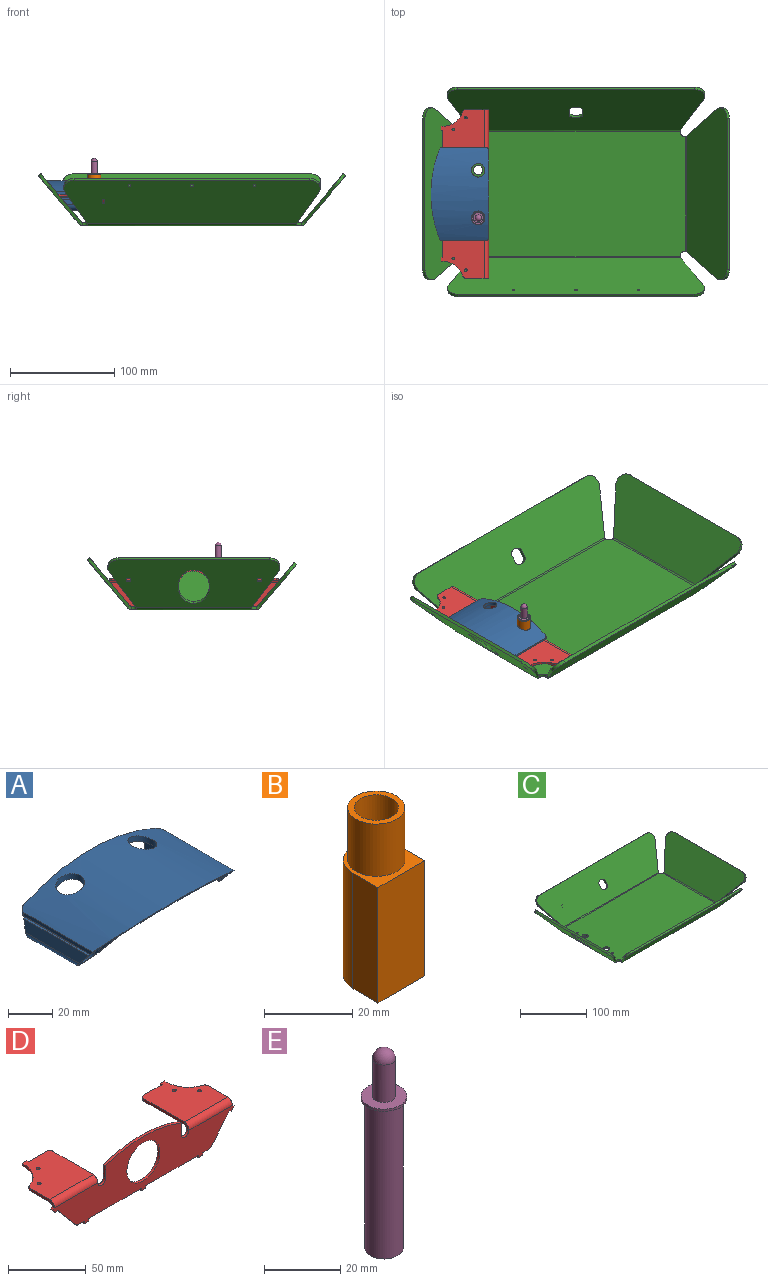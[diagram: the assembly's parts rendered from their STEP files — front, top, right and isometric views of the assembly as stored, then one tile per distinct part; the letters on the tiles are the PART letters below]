
ASSEMBLY  parts=5 mates=4
PART A: 54 faces, bbox 90.1x55.7x28.5 mm
  f0: plane 12.62x12mm, normal (-1,0,0), area 123.6mm2, adj f11,f12,f14,f30,f36,f42,f46,f48
  f1: plane 10x3.5mm, normal (0,0,-1), area 35mm2, adj f8,f13,f46,f47
  f2: plane 40.48x4mm, normal (1,0,0), area 99.5mm2, adj f3,f13,f31,f44,f46,f47
  f3: plane 90.07x28.52mm, normal (0,-0.77,-0.64), area 495.1mm2, adj f2,f15,f16,f17,f18,f19,f20,f21
  f4: cylinder r=1.5mm len=12mm, axis (0,1,0), area 56.5mm2, adj f5,f10,f42,f46
  f5: plane 12x2.1mm, normal (1,0,0), area 25.2mm2, adj f4,f6,f42,f46
  f6: cylinder r=1.5mm len=12mm, axis (0,1,0), area 22.2mm2, adj f5,f7,f42,f46
  f7: plane 12x4.99mm, normal (1,0,0), area 55.6mm2, adj f6,f11,f12,f42,f46,f48
  f8: plane 12x4.99mm, normal (-1,0,0), area 55.6mm2, adj f1,f9,f13,f41,f42,f46
  f9: cylinder r=1.5mm len=12mm, axis (0,1,0), area 22.2mm2, adj f8,f10,f42,f46
  f10: plane 12x2.1mm, normal (-1,0,0), area 25.2mm2, adj f4,f9,f42,f46
  f11: plane 5.6x3mm, normal (0,1,0), area 7mm2, adj f0,f7,f12,f48
  f12: cylinder r=3.5mm len=3.46mm, axis (0,-1,0), area 10mm2, adj f0,f7,f11,f42
  f13: plane 7.9x6.5mm, normal (0,1,0), area 33.7mm2, adj f1,f2,f8,f31,f32,f40,f41,f47
  f14: plane 78.57x27.36mm, normal (0,1,0), area 209.8mm2, adj f0,f21,f22,f23,f24,f25,f26,f27
  f15: cylinder r=100mm len=90mm, axis (0,1,0), area 4630.2mm2, adj f3,f16,f35,f42,f50,f51,f52,f53
  f16: plane 43.65x2mm, normal (-1,0,0), area 85.6mm2, adj f3,f15,f17,f51
  f17: plane 44.98x3.49mm, normal (0,0,-1), area 155.1mm2, adj f3,f16,f18,f42,f51
  f18: plane 44.98x1.5mm, normal (-1,0,0), area 66.5mm2, adj f3,f17,f19,f39,f42
  f19: plane 41.73x3.68mm, normal (0,0,-1), area 153.6mm2, adj f3,f18,f20,f43
  f20: plane 44.65x3.5mm, normal (1,0,0.01), area 151.2mm2, adj f3,f19,f21,f43
  f21: cylinder r=97mm len=46.45mm, axis (0,1,0), area 272.4mm2, adj f3,f14,f20,f22,f43
  f22: plane 46.45x14.02mm, normal (-1,0,0.05), area 569.8mm2, adj f3,f14,f21,f23
  f23: cylinder r=4.09mm len=34.78mm, axis (0,1,0), area 396.8mm2, adj f3,f14,f22,f24
  f24: plane 41.29x8.14mm, normal (0.99,0,0.12), area 310.7mm2, adj f3,f14,f23,f25
  f25: plane 41.3x1.08mm, normal (0.02,0,1), area 44.6mm2, adj f3,f14,f24,f26
  f26: plane 41.3x0.9mm, normal (-0.28,0,0.96), area 38.8mm2, adj f3,f14,f25,f27
  f27: plane 41.08x8.14mm, normal (-0.99,0,-0.12), area 309.1mm2, adj f3,f14,f26,f28
  f28: cylinder r=6.09mm len=34.7mm, axis (0,1,0), area 570.7mm2, adj f3,f14,f27,f29
  f29: plane 47.03x14.8mm, normal (1,0,-0.05), area 605.4mm2, adj f3,f14,f28,f30
  f30: cylinder r=97mm len=69.62mm, axis (0,1,0), area 3178.6mm2, adj f0,f3,f14,f29,f45,f46,f52,f53
  f31: plane 41.23x2.7mm, normal (0.32,0,0.95), area 116.3mm2, adj f2,f3,f13,f32
  f32: plane 41.23x1mm, normal (0,0,1), area 41.2mm2, adj f3,f13,f31,f33
  f33: plane 44.98x2.1mm, normal (1,0,0), area 92.6mm2, adj f3,f32,f34,f40,f42
  f34: plane 44.98x3.7mm, normal (0,0,-1), area 164.5mm2, adj f3,f33,f35,f42,f50
  f35: plane 43.65x2mm, normal (1,0,0), area 85.6mm2, adj f3,f15,f34,f50
  f36: cylinder r=99mm len=69mm, axis (0,-1,0), area 141mm2, adj f0,f14,f37,f42
  f37: plane 9.56x2mm, normal (1,0,0), area 19.1mm2, adj f14,f36,f38,f42,f43
  f38: cylinder r=3.5mm len=7mm, axis (0,-1,0), area 22mm2, adj f37,f39,f42,f43
  f39: plane 2.9x2mm, normal (-1,0,0), area 5.8mm2, adj f18,f38,f42,f43
  f40: plane 2.3x2mm, normal (1,0,0.09), area 4.6mm2, adj f13,f33,f41,f42
  f41: cylinder r=3.5mm len=3.46mm, axis (0,-1,0), area 10mm2, adj f8,f13,f40,f42
  f42: plane 84x20.6mm, normal (0,1,0), area 236.5mm2, adj f0,f4,f5,f6,f7,f8,f9,f10
  f43: plane 11.25x7.01mm, normal (0,-1,0), area 53.6mm2, adj f19,f20,f21,f37,f38,f39
  f44: plane 28.81x2.35mm, normal (0,0,-1), area 67.7mm2, adj f2,f3,f46,f49
  f45: plane 34.11x3.61mm, normal (-1,0,-0.08), area 118.1mm2, adj f3,f30,f46,f49
  f46: plane 13.35x10.5mm, normal (0,-1,0), area 69.4mm2, adj f0,f1,f2,f4,f5,f6,f7,f8
  f47: cylinder r=3mm len=10mm, axis (0,1,0), area 47.1mm2, adj f1,f2,f13,f46
  f48: cylinder r=3mm len=10mm, axis (0,1,0), area 47.1mm2, adj f0,f7,f11,f46
  f49: cylinder r=3mm len=31.1mm, axis (0,1,0), area 132.3mm2, adj f3,f44,f45,f46
  f50: cylinder r=3mm len=3.45mm, axis (0,0,1), area 11.9mm2, adj f15,f34,f35,f42
  f51: cylinder r=3mm len=3.45mm, axis (0,0,-1), area 11.9mm2, adj f15,f16,f17,f42
  f52: cylinder r=6.5mm len=13mm, axis (0,0,1), area 126.1mm2, adj f15,f30
  f53: cylinder r=6.5mm len=13mm, axis (0,0,1), area 126.3mm2, adj f15,f30
PART B: 9 faces, bbox 15x15.5x46.5 mm
  f0: plane 32x8mm, normal (1,0,0), area 256mm2, adj f1,f4,f5,f6
  f1: cylinder r=7.5mm len=32mm, axis (0,0,-1), area 754mm2, adj f0,f2,f5,f6
  f2: plane 32x8mm, normal (-1,0,0), area 256mm2, adj f1,f4,f5,f6
  f3: cylinder r=5mm len=46.5mm, axis (0,0,-1), area 1460.8mm2, adj f6,f8
  f4: plane 32x15mm, normal (0,-1,0), area 480mm2, adj f0,f2,f5,f6
  f5: plane 15.5x15mm, normal (0,0,1), area 75.6mm2, adj f0,f1,f2,f4,f7
  f6: plane 15.5x15mm, normal (0,0,-1), area 129.8mm2, adj f0,f1,f2,f3,f4
  f7: cylinder r=6.5mm len=14.5mm, axis (0,0,-1), area 592.2mm2, adj f5,f8
  f8: plane 13x13mm, normal (0,0,1), area 54.2mm2, adj f3,f7
PART C: 97 faces, bbox 295.6x202x50.5 mm
  f0: cylinder r=1.25mm len=3mm, axis (0,0,1), area 23.6mm2, adj f15,f16
  f1: cylinder r=1.25mm len=3mm, axis (0,0,1), area 23.6mm2, adj f15,f16
  f2: cylinder r=4.5mm len=9mm, axis (0,0,1), area 84.8mm2, adj f15,f16
  f3: cylinder r=4.5mm len=9mm, axis (0,0,1), area 84.8mm2, adj f15,f16
  f4: cylinder r=8.05mm len=13.1mm, axis (0,0.77,-0.64), area 45.9mm2, adj f23,f24,f62,f63
  f5: cylinder r=1.25mm len=3.91mm, axis (0,-0.77,-0.64), area 23.6mm2, adj f48,f49
  f6: cylinder r=1.25mm len=3.91mm, axis (0,-0.77,-0.64), area 23.6mm2, adj f48,f49
  f7: cylinder r=1.25mm len=3.91mm, axis (0,-0.77,-0.64), area 23.6mm2, adj f48,f49
  f8: extruded ~17.89x15.69mm, area 85.6mm2, adj f9,f10,f51,f52
  f9: plane 166.16x46.71mm, normal (-0.77,0,-0.64), area 7583.8mm2, adj f8,f28,f30,f31,f32,f51,f52,f53
  f10: plane 166.16x46.71mm, normal (0.77,0,0.64), area 7583.8mm2, adj f8,f29,f30,f31,f32,f51,f52,f53
  f11: cylinder r=5mm len=5mm, axis (0,0,1), area 23.6mm2, adj f15,f16,f18,f26
  f12: cylinder r=5mm len=5mm, axis (0,0,1), area 23.6mm2, adj f15,f16,f17,f34
  f13: cylinder r=5mm len=5mm, axis (0,0,1), area 23.6mm2, adj f15,f16,f33,f43
  f14: cylinder r=5mm len=5mm, axis (0,0,1), area 23.6mm2, adj f15,f16,f27,f42
  f15: plane 210x120mm, normal (0,0,-1), area 24956.7mm2, adj f0,f1,f2,f3,f11,f12,f13,f14
  f16: plane 210x120mm, normal (0,0,1), area 24984.4mm2, adj f0,f1,f2,f3,f11,f12,f13,f14
  f17: bspline ~3.85x3.74mm, area 9.3mm2, adj f12,f19,f20,f21
  f18: bspline ~3.85x3.74mm, area 9.3mm2, adj f11,f19,f20,f22
  f19: cylinder r=5mm len=200.92mm, axis (-1,0,0), area 874.7mm2, adj f15,f17,f18,f23
  f20: cylinder r=2mm len=200.92mm, axis (-1,0,0), area 349.9mm2, adj f16,f17,f18,f24
  f21: plane 36.9x31.64mm, normal (0.9,-0.28,-0.34), area 152.6mm2, adj f17,f23,f24,f58
  f22: plane 36.9x31.64mm, normal (-0.9,-0.28,-0.34), area 152.6mm2, adj f18,f23,f24,f59
  f23: plane 247.88x46.01mm, normal (0,0.77,-0.64), area 13530.9mm2, adj f4,f19,f21,f22,f25,f58,f59,f61
  f24: plane 247.88x46.01mm, normal (0,-0.77,0.64), area 13540.1mm2, adj f4,f20,f21,f22,f25,f58,f59,f61
  f25: plane 227.88x2.3mm, normal (0,0.64,0.77), area 683.6mm2, adj f23,f24,f58,f59
  f26: bspline ~3.85x3.74mm, area 9.3mm2, adj f11,f28,f29,f30
  f27: bspline ~3.83x3.71mm, area 9.3mm2, adj f14,f28,f29,f31
  f28: cylinder r=5mm len=111.07mm, axis (0,-1,0), area 482.3mm2, adj f9,f15,f26,f27
  f29: cylinder r=2mm len=111.07mm, axis (0,-1,0), area 192.9mm2, adj f10,f16,f26,f27
  f30: plane 36.47x31.28mm, normal (0.32,0.87,-0.38), area 156mm2, adj f9,f10,f26,f60
  f31: plane 36.47x31.28mm, normal (0.32,-0.87,-0.38), area 156mm2, adj f9,f10,f27,f53
  f32: plane 145.47x2.3mm, normal (-0.64,0,0.77), area 436.4mm2, adj f9,f10,f53,f60
  f33: bspline ~3.85x3.74mm, area 9.3mm2, adj f13,f35,f36,f37
  f34: bspline ~3.83x3.71mm, area 9.3mm2, adj f12,f35,f36,f38
  f35: cylinder r=5mm len=111.07mm, axis (0,1,0), area 482.3mm2, adj f15,f33,f34,f39
  f36: cylinder r=2mm len=111.07mm, axis (0,1,0), area 192.9mm2, adj f16,f33,f34,f40
  f37: plane 36.47x31.28mm, normal (-0.32,-0.87,-0.38), area 156mm2, adj f33,f39,f40,f56
  f38: plane 36.47x31.28mm, normal (-0.32,0.87,-0.38), area 156mm2, adj f34,f39,f40,f57
  f39: plane 165.47x46.01mm, normal (0.77,0,-0.64), area 8605.7mm2, adj f35,f37,f38,f41,f56,f57
  f40: plane 165.47x46.01mm, normal (-0.77,0,0.64), area 8605.7mm2, adj f36,f37,f38,f41,f56,f57
  f41: plane 145.47x2.3mm, normal (0.64,0,0.77), area 436.4mm2, adj f39,f40,f56,f57
  f42: bspline ~3.85x3.74mm, area 9.3mm2, adj f14,f44,f45,f46
  f43: bspline ~3.83x3.71mm, area 9.3mm2, adj f13,f44,f45,f47
  f44: cylinder r=5mm len=201.01mm, axis (1,0,0), area 874.9mm2, adj f15,f42,f43,f48
  f45: cylinder r=2mm len=201.01mm, axis (1,0,0), area 349.9mm2, adj f16,f42,f43,f49
  f46: plane 32.43x27.89mm, normal (-0.88,0.31,-0.36), area 135.8mm2, adj f42,f48,f49,f54
  f47: plane 32.43x27.89mm, normal (0.88,0.31,-0.36), area 135.8mm2, adj f43,f48,f49,f55
  f48: plane 246.45x41.8mm, normal (0,-0.77,-0.64), area 12425.2mm2, adj f5,f6,f7,f44,f46,f47,f50,f54
  f49: plane 246.45x41.8mm, normal (0,0.77,0.64), area 12434.5mm2, adj f5,f6,f7,f45,f46,f47,f50,f54
  f50: plane 226.45x2.3mm, normal (0,-0.64,0.77), area 679.4mm2, adj f48,f49,f54,f55
  f51: extruded ~17.89x15.69mm, area 85.6mm2, adj f8,f9,f10,f52
  f52: extruded ~29.99x17.89mm, area 171.3mm2, adj f8,f9,f10,f51
  f53: cylinder r=10mm len=13.4mm, axis (0.77,0,0.64), area 62.8mm2, adj f9,f10,f31,f32
  f54: cylinder r=10mm len=13.23mm, axis (0,0.77,0.64), area 62mm2, adj f46,f48,f49,f50
  f55: cylinder r=10mm len=13.23mm, axis (0,0.77,0.64), area 62mm2, adj f47,f48,f49,f50
  f56: cylinder r=10mm len=13.4mm, axis (-0.77,0,0.64), area 62.8mm2, adj f37,f39,f40,f41
  f57: cylinder r=10mm len=13.4mm, axis (-0.77,0,0.64), area 62.8mm2, adj f38,f39,f40,f41
  f58: cylinder r=10mm len=12.97mm, axis (0,-0.77,0.64), area 60.8mm2, adj f21,f23,f24,f25
  f59: cylinder r=10mm len=12.97mm, axis (0,-0.77,0.64), area 60.8mm2, adj f22,f23,f24,f25
  f60: cylinder r=10mm len=13.4mm, axis (0.77,0,0.64), area 62.8mm2, adj f9,f10,f30,f32
  f61: cylinder r=8.05mm len=13.1mm, axis (0,0.77,-0.64), area 45.9mm2, adj f23,f24,f62,f63
  f62: plane 9.1x8.31mm, normal (-1,0,0), area 28.1mm2, adj f4,f23,f24,f61
  f63: plane 9.1x8.31mm, normal (1,0,0), area 28.1mm2, adj f4,f23,f24,f61
  f64: plane 2.2x2mm, normal (0,-1,0), area 4.4mm2, adj f15,f65,f67,f68
  f65: plane 4.2x2mm, normal (1,0,0), area 8.4mm2, adj f15,f64,f66,f68
  f66: plane 2.2x2mm, normal (0,1,0), area 4.4mm2, adj f15,f65,f67,f68
  f67: plane 4.2x2mm, normal (-1,0,0), area 8.4mm2, adj f15,f64,f66,f68
  f68: plane 4.2x2.2mm, normal (0,0,-1), area 9.2mm2, adj f64,f65,f66,f67
  f69: plane 2.2x2mm, normal (0,-1,0), area 4.4mm2, adj f15,f70,f72,f73
  f70: plane 4.2x2mm, normal (1,0,0), area 8.4mm2, adj f15,f69,f71,f73
  f71: plane 2.2x2mm, normal (0,1,0), area 4.4mm2, adj f15,f70,f72,f73
  f72: plane 4.2x2mm, normal (-1,0,0), area 8.4mm2, adj f15,f69,f71,f73
  f73: plane 4.2x2.2mm, normal (0,0,-1), area 9.2mm2, adj f69,f70,f71,f72
  f74: plane 2.2x2mm, normal (0,-1,0), area 4.4mm2, adj f15,f75,f77,f78
  f75: plane 4.2x2mm, normal (1,0,0), area 8.4mm2, adj f15,f74,f76,f78
  f76: plane 2.2x2mm, normal (0,1,0), area 4.4mm2, adj f15,f75,f77,f78
  f77: plane 4.2x2mm, normal (-1,0,0), area 8.4mm2, adj f15,f74,f76,f78
  f78: plane 4.2x2.2mm, normal (0,0,-1), area 9.2mm2, adj f74,f75,f76,f77
  f79: plane 2.2x1.53mm, normal (0,-0.64,-0.77), area 4.4mm2, adj f23,f80,f82,f83
  f80: plane 4.5x4.23mm, normal (1,0,0), area 8.4mm2, adj f23,f79,f81,f83
  f81: plane 2.2x1.53mm, normal (0,0.64,0.77), area 4.4mm2, adj f23,f80,f82,f83
  f82: plane 4.5x4.23mm, normal (-1,0,0), area 8.4mm2, adj f23,f79,f81,f83
  f83: plane 3.22x2.7mm, normal (0,0.77,-0.64), area 9.2mm2, adj f79,f80,f81,f82
  f84: plane 2.2x1.53mm, normal (0,-0.64,0.77), area 4.4mm2, adj f48,f85,f87,f88
  f85: plane 4.5x4.23mm, normal (1,0,0), area 8.4mm2, adj f48,f84,f86,f88
  f86: plane 2.2x1.53mm, normal (0,0.64,-0.77), area 4.4mm2, adj f48,f85,f87,f88
  f87: plane 4.5x4.23mm, normal (-1,0,0), area 8.4mm2, adj f48,f84,f86,f88
  f88: plane 3.22x2.7mm, normal (0,-0.77,-0.64), area 9.2mm2, adj f84,f85,f86,f87
  f89: plane 4.12x4.1mm, normal (0,1,0), area 8.5mm2, adj f9,f10,f90,f92
  f90: plane 4.2x2.3mm, normal (-0.64,0,0.77), area 12.6mm2, adj f9,f10,f89,f91
  f91: plane 4.12x4.1mm, normal (0,-1,0), area 8.5mm2, adj f9,f10,f90,f92
  f92: plane 4.2x2.3mm, normal (0.64,0,-0.77), area 12.6mm2, adj f9,f10,f89,f91
  f93: plane 4.12x4.1mm, normal (0,-1,0), area 8.5mm2, adj f9,f10,f94,f96
  f94: plane 4.2x2.3mm, normal (0.64,0,-0.77), area 12.6mm2, adj f9,f10,f93,f95
  f95: plane 4.12x4.1mm, normal (0,1,0), area 8.5mm2, adj f9,f10,f94,f96
  f96: plane 4.2x2.3mm, normal (-0.64,0,0.77), area 12.6mm2, adj f9,f10,f93,f95
PART D: 65 faces, bbox 165.2x45.8x42 mm
  f0: plane 41.4x39.57mm, normal (0,0,1), area 1324.3mm2, adj f2,f3,f41,f43,f55,f56,f57,f58
  f1: plane 41.4x39.57mm, normal (0,0,-1), area 1324.3mm2, adj f2,f3,f42,f43,f55,f56,f57,f58
  f2: plane 17.65x2mm, normal (-1,0,0), area 35.3mm2, adj f0,f1,f39,f61
  f3: plane 16.45x2mm, normal (0,1,0), area 32.9mm2, adj f0,f1,f59,f62
  f4: plane 16.45x2mm, normal (0,1,0), area 32.9mm2, adj f5,f6,f53,f64
  f5: plane 41.4x39.57mm, normal (0,0,1), area 1324.3mm2, adj f4,f7,f46,f48,f49,f50,f51,f52
  f6: plane 41.4x39.57mm, normal (0,0,-1), area 1324.3mm2, adj f4,f7,f47,f48,f49,f50,f51,f52
  f7: plane 17.65x2mm, normal (1,0,0), area 35.3mm2, adj f5,f6,f45,f63
  f8: plane 2x1.53mm, normal (-0.64,0,0.77), area 4mm2, adj f35,f36,f37,f39
  f9: cylinder r=3.5mm len=7mm, axis (0,-1,0), area 22mm2, adj f10,f36,f37,f40
  f10: plane 10.02x2mm, normal (-1,0,0), area 20mm2, adj f9,f11,f36,f37
  f11: cylinder r=99mm len=69mm, axis (0,-1,0), area 141mm2, adj f10,f12,f36,f37
  f12: plane 9.56x2mm, normal (1,0,0), area 19.1mm2, adj f11,f13,f36,f37
  f13: cylinder r=3.5mm len=7mm, axis (0,-1,0), area 22mm2, adj f12,f36,f37,f44
  f14: plane 2x1.53mm, normal (0.64,0,0.77), area 4mm2, adj f15,f36,f37,f45
  f15: plane 3.06x2.57mm, normal (0.77,0,-0.64), area 8mm2, adj f14,f16,f36,f37
  f16: plane 2x1.53mm, normal (-0.64,0,-0.77), area 4mm2, adj f15,f17,f36,f37
  f17: plane 19.65x16.49mm, normal (0.77,0,-0.64), area 51.3mm2, adj f16,f18,f36,f37
  f18: cylinder r=3.6mm len=2.76mm, axis (0,-1,0), area 6.3mm2, adj f17,f19,f36,f37
  f19: plane 5.25x2mm, normal (0,0,-1), area 10.5mm2, adj f18,f20,f36,f37
  f20: plane 2x2mm, normal (1,0,0), area 4mm2, adj f19,f21,f36,f37
  f21: plane 4x2mm, normal (0,0,-1), area 8mm2, adj f20,f22,f36,f37
  f22: plane 2x2mm, normal (-1,0,0), area 4mm2, adj f21,f23,f36,f37
  f23: plane 48x2mm, normal (0,0,-1), area 96mm2, adj f22,f24,f36,f37
  f24: plane 2x2mm, normal (1,0,0), area 4mm2, adj f23,f25,f36,f37
  f25: plane 4x2mm, normal (0,0,-1), area 8mm2, adj f24,f26,f36,f37
  f26: plane 2x2mm, normal (-1,0,0), area 4mm2, adj f25,f27,f36,f37
  f27: plane 48x2mm, normal (0,0,-1), area 96mm2, adj f26,f28,f36,f37
  f28: plane 2x2mm, normal (1,0,0), area 4mm2, adj f27,f29,f36,f37
  f29: plane 4x2mm, normal (0,0,-1), area 8mm2, adj f28,f30,f36,f37
  f30: plane 2x2mm, normal (-1,0,0), area 4mm2, adj f29,f31,f36,f37
  f31: plane 5.25x2mm, normal (0,0,-1), area 10.5mm2, adj f30,f32,f36,f37
  f32: cylinder r=3.6mm len=2.76mm, axis (0,-1,0), area 6.3mm2, adj f31,f33,f36,f37
  f33: plane 19.65x16.49mm, normal (-0.77,0,-0.64), area 51.3mm2, adj f32,f34,f36,f37
  f34: plane 2x1.53mm, normal (0.64,0,-0.77), area 4mm2, adj f33,f35,f36,f37
  f35: plane 3.06x2.57mm, normal (-0.77,0,-0.64), area 8mm2, adj f8,f34,f36,f37
  f36: plane 165.21x42mm, normal (0,1,0), area 3655.5mm2, adj f8,f9,f10,f11,f12,f13,f14,f15
  f37: plane 165.21x42mm, normal (0,-1,0), area 3655.5mm2, adj f8,f9,f10,f11,f12,f13,f14,f15
  f38: cylinder r=15.1mm len=30.2mm, axis (0,-1,0), area 189.8mm2, adj f36,f37
  f39: plane 4.4x4.4mm, normal (-1,0,0), area 10.7mm2, adj f2,f8,f41,f42
  f40: plane 4.4x4.4mm, normal (1,0,0), area 10.7mm2, adj f9,f41,f42,f43
  f41: cylinder r=4.4mm len=39.57mm, axis (1,0,0), area 273.5mm2, adj f0,f37,f39,f40
  f42: cylinder r=2.4mm len=39.57mm, axis (1,0,0), area 149.2mm2, adj f1,f36,f39,f40
  f43: plane 36.6x2mm, normal (1,0,0), area 73.2mm2, adj f0,f1,f40,f62
  f44: plane 4.4x4.4mm, normal (-1,0,0), area 10.7mm2, adj f13,f46,f47,f48
  f45: plane 4.4x4.4mm, normal (1,0,0), area 10.7mm2, adj f7,f14,f46,f47
  f46: cylinder r=4.4mm len=39.57mm, axis (1,0,0), area 273.5mm2, adj f5,f37,f44,f45
  f47: cylinder r=2.4mm len=39.57mm, axis (1,0,0), area 149.2mm2, adj f6,f36,f44,f45
  f48: plane 36.6x2mm, normal (-1,0,0), area 73.2mm2, adj f5,f6,f44,f64
  f49: cylinder r=1.25mm len=2.5mm, axis (0,0,-1), area 15.7mm2, adj f5,f6
  f50: cylinder r=1.25mm len=2.5mm, axis (0,0,-1), area 15.7mm2, adj f5,f6
  f51: cylinder r=20mm len=19.09mm, axis (0,0,-1), area 50.7mm2, adj f5,f6,f52,f63
  f52: plane 2x1.8mm, normal (1,0,0), area 3.6mm2, adj f5,f6,f51,f54
  f53: plane 2x1.8mm, normal (-1,0,0), area 3.6mm2, adj f4,f5,f6,f54
  f54: plane 4x2mm, normal (0,1,0), area 8mm2, adj f5,f6,f52,f53
  f55: cylinder r=1.25mm len=2.5mm, axis (0,0,1), area 15.7mm2, adj f0,f1
  f56: cylinder r=1.25mm len=2.5mm, axis (0,0,1), area 15.7mm2, adj f0,f1
  f57: cylinder r=20mm len=19.09mm, axis (0,0,-1), area 50.7mm2, adj f0,f1,f58,f61
  f58: plane 2x1.8mm, normal (-1,0,0), area 3.6mm2, adj f0,f1,f57,f60
  f59: plane 2x1.8mm, normal (1,0,0), area 3.6mm2, adj f0,f1,f3,f60
  f60: plane 4x2mm, normal (0,1,0), area 8mm2, adj f0,f1,f58,f59
  f61: cylinder r=3mm len=2.86mm, axis (0,0,-1), area 7.6mm2, adj f0,f1,f2,f57
  f62: cylinder r=3mm len=3mm, axis (0,0,-1), area 9.4mm2, adj f0,f1,f3,f43
  f63: cylinder r=3mm len=2.86mm, axis (0,0,-1), area 7.6mm2, adj f5,f6,f7,f51
  f64: cylinder r=3mm len=3mm, axis (0,0,-1), area 9.4mm2, adj f4,f5,f6,f48
PART E: 7 faces, bbox 12x12x63.7 mm
  f0: plane 12x12mm, normal (0,0,1), area 84.8mm2, adj f4,f5
  f1: cylinder r=5mm len=48mm, axis (0,0,-1), area 1508mm2, adj f2,f3
  f2: plane 10x10mm, normal (0,0,-1), area 78.5mm2, adj f1
  f3: plane 12x12mm, normal (0,0,-1), area 34.6mm2, adj f1,f4
  f4: cylinder r=6mm len=12mm, axis (0,0,-1), area 26.4mm2, adj f0,f3
  f5: cylinder r=3mm len=12mm, axis (0,0,-1), area 226.2mm2, adj f0,f6
  f6: sphere r=3mm, area 56.5mm2, adj f5
PLACE A rot(axis=(0,0,-1),90deg) t=(-86.52,2.21,39.37)mm
PLACE B rot(axis=(0,0,1),90deg) t=(-94.52,-20.5,0)mm
PLACE C t=(-0.52,2.5,0)mm
PLACE D rot(axis=(0,0,1),90deg) t=(-84.52,1.87,-104)mm
PLACE E t=(194.74,83.49,-1.99)mm
MATE fastened A.f38 <-> D.f13  axis (1,0,0) through (-84.52,40.5,23)mm
MATE fastened B.f3 <-> C.f3  axis (0,0,-1) through (-94.52,-20.5,0)mm
MATE fastened D.f25 <-> C.f15  axis (0,0,-1) through (-85.52,2.5,-3)mm
MATE slider E.f1 <-> A.f53  axis (0,0,-1) through (-94.52,-20.85,22.01)mm
